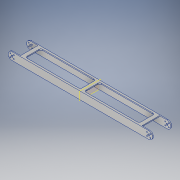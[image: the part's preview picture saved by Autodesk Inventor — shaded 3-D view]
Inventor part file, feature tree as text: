
AUTODESK INVENTOR PART (.ipt)
format: ipt  version: 2017 (Build 210142000, 142)  size: 239,616 bytes
history: native  units: in
note: dims shown in document units (in); Inventor stores cm internally (conversion verified against a paired STEP export)
features: sketch x5, extrude x4, fillet x3, projected_geometry x3, hole x1, plane x1, mirror x1
ambient origin geometry x8: Origin, YZ Plane, XZ Plane, XY Plane, X Axis, Y Axis, Z Axis, Center Point
bodies: Solid1 (feature_tree)
feature tree (18):
  extrude  "Extrusion1"  Depth=2.2935in
  extrude  "Extrusion2"  Depth=0.125in
  extrude  "Extrusion3"  Depth=2.5435in
  hole  "Hole1"  [1 undecoded]
  fillet  "Fillet1"  Radius=0.25in
  extrude  "Extrusion4"  Depth=1.0in
  fillet  "Fillet2"  Radius=0.5in
  plane  "Work Plane1"
  mirror  "Mirror1"
  fillet  "Fillet3"  Radius=0.25in
  sketch  "Sketch1"  dims[d0=1.0in d2=2.2935in]
  sketch  "Sketch3"  dims[d3=0.875in d4=0.125in]
  projected_geometry  "Projected Loop2"
  sketch  "Sketch4"  dims[d5=19.0in d6=0.0in d14=2.5435in]
  projected_geometry  "Projected Loop3"
  sketch  "Sketch5"  dims[d16=1.5in d17=0.125in d18=0.0in d19=0.25in]
  sketch  "Sketch6"  dims[d20=0.5in d21=1.0in d22=0.5in d23=0.25in d24=0.5in d25=5.0in d26=0.0in d27=1.5in d28=2.2935in d29=0.125in d30=2.2935in d31=0.125in d32=0.125in d33=0.445in d34=0.445in d35=0.2775in d36=0.2775in d37=0.445in d38=0.445in d39=0.2775in d40=0.2775in d43=1.0003in d47=0.445in d48=0.445in d49=0.2777in d50=0.2777in d51=0.445in d52=0.445in d53=0.2777in d55=0.1378in d56=0.75in d57=0.375in d58=0.25in d59=0.5635in d60=5.0in d61=0.8108in d62=0.5in d63=0.7227in d65=16.0in d66=2.5435in d67=0.25in d68=2.0435in d69=0.5in d70=7.25in d71=1.0in d72=0.0in d73=0.25in d74=0.25in]
  projected_geometry  "Projected Loop4"
note: 1 required parameter value undecoded (feature->parameter linkage not recoverable at this tier; creation-order binding heuristic only, values carry confidence <= 0.55)
